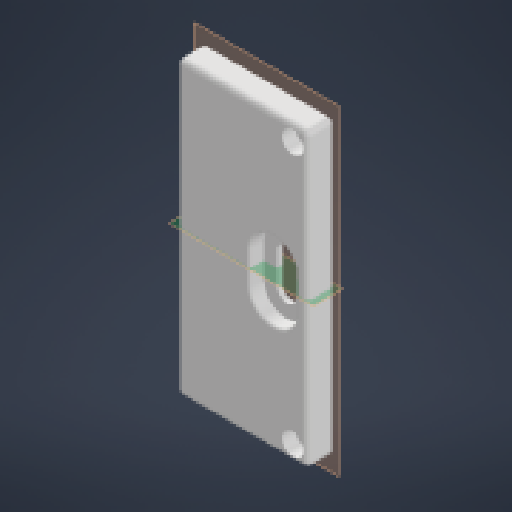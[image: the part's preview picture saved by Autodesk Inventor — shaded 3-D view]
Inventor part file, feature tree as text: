
AUTODESK INVENTOR PART (.ipt)
format: ipt  version: 2023 (Build 270158000, 158)  size: 310,272 bytes
history: native  units: mm
features: reference x15, extrude x12, sketch x12, plane x3, projected_geometry x3, other x3, fillet x2, mirror x1
ambient origin geometry x8: Origin, YZ Plane, XZ Plane, XY Plane, X Axis, Y Axis, Z Axis, Center Point
bodies: Solid1 (feature_tree)
feature tree (51):
  plane  "Work Plane1"
  extrude  "Extrusion1"  Depth=4.5mm TaperAngle=0.0deg
  extrude  "Extrusion2"  Depth=2.5mm
  extrude  "Extrusion3"  Depth=2.5mm TaperAngle=0.0deg
  extrude  "Extrusion4"  Depth=4.0mm
  extrude  "Extrusion5"  Depth=2.5mm
  extrude  "Extrusion6"  Depth=30.0mm
  extrude  "Extrusion7"  Depth=9.0mm
  extrude  "Extrusion8"  Depth=2.5mm TaperAngle=0.0deg
  extrude  "Extrusion9"  Depth=2.5mm TaperAngle=0.0deg
  extrude  "Extrusion10"  Depth=0.5mm TaperAngle=0.0deg
  sketch  "Sketch11"  dims[d29=0.75mm d30=0.5mm d31=0.0mm]
  plane  "Work Plane2"
  extrude  "Extrusion11"  Depth=0.5mm TaperAngle=0.0deg
  extrude  "Extrusion12"  Depth=10.0mm TaperAngle=0.0deg
  plane  "Work Plane3"
  mirror  "Mirror1"
  fillet  "Fillet1"  Radius=1.0mm
  fillet  "Fillet2"  Radius=0.5mm
  sketch  "Sketch1"  dims[d0=4.5mm d1=0.0mm d2=3.5mm d3=0.0mm]
  reference  "Reference1"
  sketch  "Sketch2"  dims[d4=2.5mm d5=0.0mm d6=2.2mm]
  projected_geometry  "Projected Loop1"
  sketch  "Sketch3"  dims[d7=2.2mm d8=2.5mm d9=0.0mm]
  reference  "Reference2"
  sketch  "Sketch4"  dims[d10=4.0mm d11=4.0mm]
  reference  "Reference3"
  reference  "Reference4"
  sketch  "Sketch5"  dims[d12=2.5mm d13=0.0mm d14=46.8mm]
  sketch  "Sketch6"  dims[d15=30.0mm d16=30.0mm]
  reference  "Reference5"
  reference  "Reference6"
  reference  "Reference7"
  reference  "Reference8"
  reference  "Reference9"
  sketch  "Sketch7"  dims[d17=3.2mm d18=9.0mm]
  projected_geometry  "Projected Loop2"
  sketch  "Sketch8"  dims[d19=0.2mm d20=2.5mm d21=0.0mm]
  sketch  "Sketch9"  dims[d22=8.5mm d23=2.5mm d24=0.0mm]
  reference  "Reference10"
  reference  "Reference11"
  reference  "Reference12"
  reference  "Reference13"
  sketch  "Sketch10"  dims[d25=1.0mm d26=0.0mm d27=0.5mm d28=0.0mm]
  reference  "Reference14"
  sketch  "Sketch12"  dims[d32=5.0mm d33=0.0mm d34=10.0mm d35=0.0mm d36=1.0mm d37=0.5mm]
  projected_geometry  "Projected Loop3"
  reference  "Reference15"
  other  "<userpath>\Documents\Assembly1.iam"
  other  "Assembly1.iam"
  other  "V1.0 Case:1"
